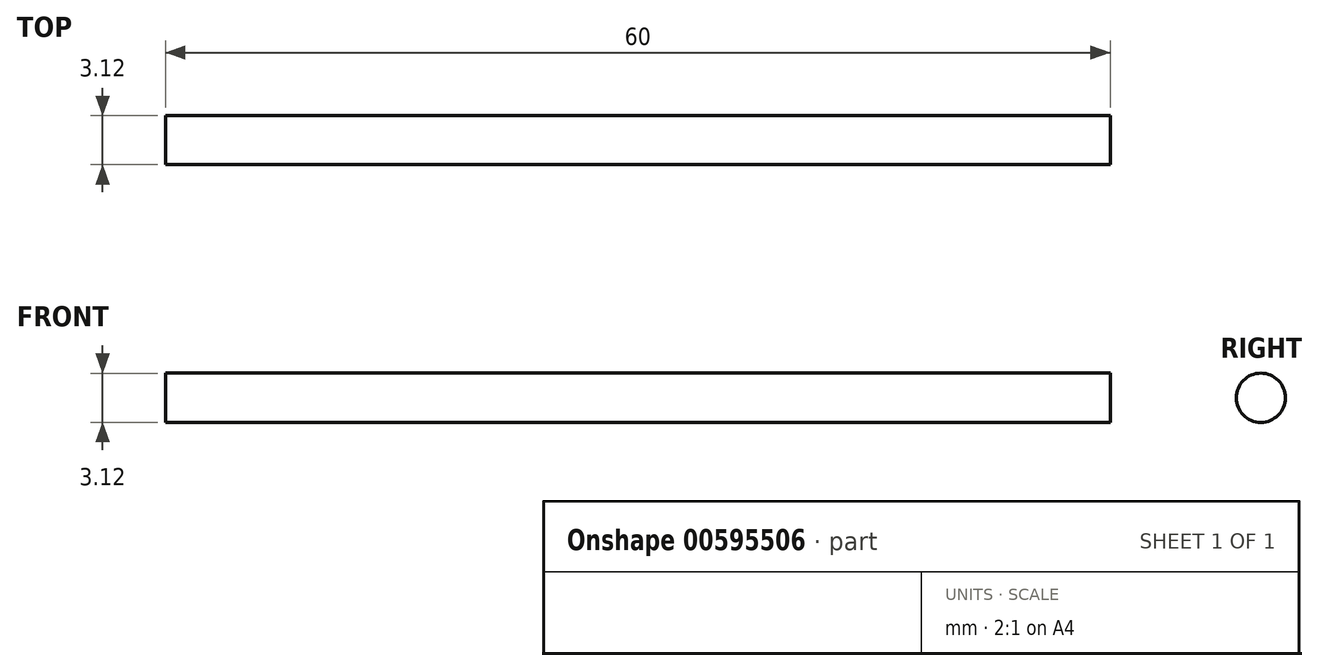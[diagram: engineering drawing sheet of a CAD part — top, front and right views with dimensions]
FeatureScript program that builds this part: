
annotation { "Feature Type Name" : "Feature", "Feature Type Description" : "" }
export const myFeature = defineFeature(function(context is Context, id is Id, definition is map)
    precondition{}
    {
        {
            var Q0;
            Q0=qCreatedBy(makeId("Right.planeOp"),FACE);
            var sketch = newSketch(context, id + "F0", { "sketchPlane" : qUnion([Q0])});
            skCircle(sketch, "E0", {"center": v(0, 0) * mm, "radius": 1.56 * mm});
            skSolve(sketch);
        }
        {
            var Q0;
            Q0=makeQuery(id+"F0.imprint","IMPRINT",FACE,{"disambiguationData":[TD([[makeQuery(id+"F0.imprint","IMPRINT",EDGE,{"derivedFrom":sQuery(id+"F0.wireOp",EDGE,"E0")}),1.0]])]});
            extrude(context, id + "F1", {"entities" : qUnion([Q0]), "depth" : 60 * mm, "offsetDistance" : 25 * mm});
        }
    });
